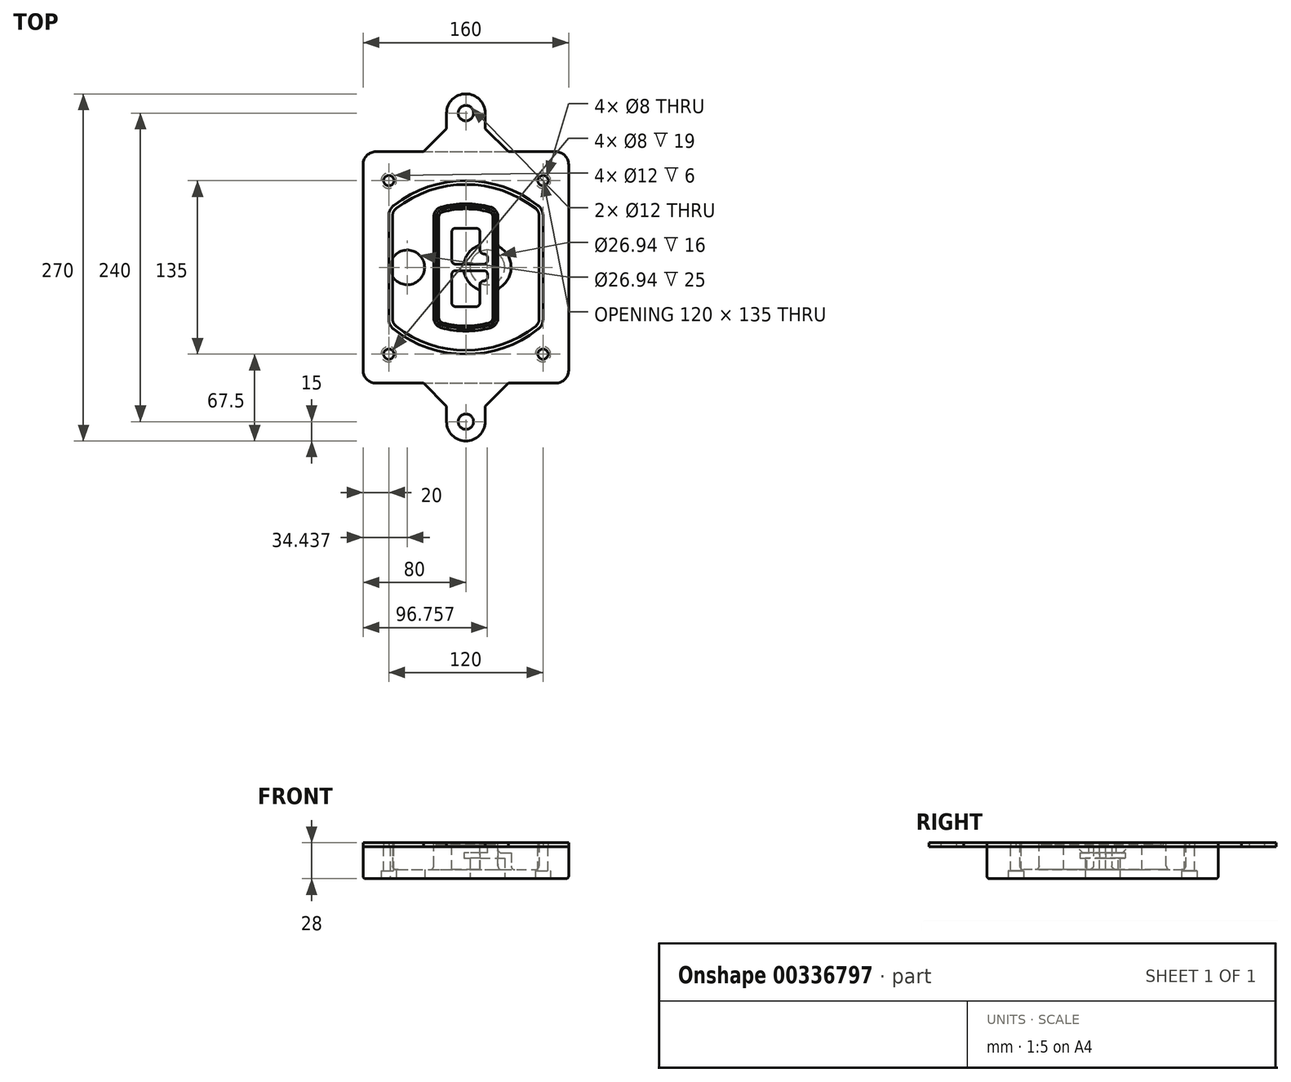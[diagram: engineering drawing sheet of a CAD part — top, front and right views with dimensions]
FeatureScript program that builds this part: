
annotation { "Feature Type Name" : "Feature", "Feature Type Description" : "" }
export const myFeature = defineFeature(function(context is Context, id is Id, definition is map)
    precondition{}
    {
        {
            var Q0;
            Q0=qCreatedBy(makeId("Top.planeOp"),FACE);
            var sketch = newSketch(context, id + "F0", { "sketchPlane" : qUnion([Q0])});
            skPoint(sketch, "E0.rect.middle", {"position": v(0, 0) * mm});
            skLineSegment(sketch, "E1.bottom", {"start": v(-70, -90) * mm, "end": v(70, -90) * mm});
            skLineSegment(sketch, "E1.top", {"start": v(-70, 90) * mm, "end": v(70, 90) * mm});
            skLineSegment(sketch, "E1.left", {"start": v(-80, -80) * mm, "end": v(-80, 80) * mm});
            skLineSegment(sketch, "E1.right", {"start": v(80, -80) * mm, "end": v(80, 80) * mm});
            skLineSegment(sketch, "E2", {"start": v(-80, 90) * mm, "end": v(80, -90) * mm, "construction": true});
            skLineSegment(sketch, "E3", {"start": v(80, 90) * mm, "end": v(-80, -90) * mm, "construction": true});
            skCircle(sketch, "E4", {"center": v(-60, 67.5) * mm, "radius": 4 * mm});
            skCircle(sketch, "E5", {"center": v(60, 67.5) * mm, "radius": 4 * mm});
            skCircle(sketch, "E6", {"center": v(60, -67.5) * mm, "radius": 4 * mm});
            skCircle(sketch, "E7", {"center": v(-60, -67.5) * mm, "radius": 4 * mm});
            skLineSegment(sketch, "E8", {"start": v(-60, 67.5) * mm, "end": v(60, 67.5) * mm, "construction": true});
            skLineSegment(sketch, "E9", {"start": v(60, 67.5) * mm, "end": v(60, -67.5) * mm, "construction": true});
            skLineSegment(sketch, "E10", {"start": v(60, -67.5) * mm, "end": v(-60, -67.5) * mm, "construction": true});
            skLineSegment(sketch, "E11", {"start": v(-60, -67.5) * mm, "end": v(-60, 67.5) * mm, "construction": true});
            skLineSegment(sketch, "E12", {"start": v(-60, 40.3) * mm, "end": v(-60, -40.3) * mm});
            skLineSegment(sketch, "E13", {"start": v(60, 40.3) * mm, "end": v(60, -40.3) * mm});
            skArc(sketch, "E14", {"start": v(56.15, 48.18) * mm, "mid": v(0, 67.5) * mm, "end": v(-56.15, 48.18) * mm});
            skArc(sketch, "E15", {"start": v(-56.15, -48.18) * mm, "mid": v(0, -67.5) * mm, "end": v(56.15, -48.18) * mm});
            skLineSegment(sketch, "E16", {"start": v(-60, 0) * mm, "end": v(60, 0) * mm, "construction": true});
            skPoint(sketch, "E17.visualSharp", {"position": v(-60, -45) * mm});
            skArc(sketch, "E17.filletArc", {"start": v(-60, -40.3) * mm, "mid": v(-58.99, -44.68) * mm, "end": v(-56.15, -48.18) * mm});
            skPoint(sketch, "E18.visualSharp", {"position": v(-60, 45) * mm});
            skArc(sketch, "E18.filletArc", {"start": v(-56.15, 48.18) * mm, "mid": v(-58.99, 44.68) * mm, "end": v(-60, 40.3) * mm});
            skPoint(sketch, "E19.visualSharp", {"position": v(60, 45) * mm});
            skArc(sketch, "E19.filletArc", {"start": v(60, 40.3) * mm, "mid": v(58.99, 44.68) * mm, "end": v(56.15, 48.18) * mm});
            skPoint(sketch, "E20.visualSharp", {"position": v(60, -45) * mm});
            skArc(sketch, "E20.filletArc", {"start": v(56.15, -48.18) * mm, "mid": v(58.99, -44.68) * mm, "end": v(60, -40.3) * mm});
            skPoint(sketch, "E21.visualSharp", {"position": v(-80, 90) * mm});
            skArc(sketch, "E21.filletArc", {"start": v(-70, 90) * mm, "mid": v(-77.07, 87.07) * mm, "end": v(-80, 80) * mm});
            skPoint(sketch, "E22.visualSharp", {"position": v(80, 90) * mm});
            skArc(sketch, "E22.filletArc", {"start": v(80, 80) * mm, "mid": v(77.07, 87.07) * mm, "end": v(70, 90) * mm});
            skPoint(sketch, "E23.visualSharp", {"position": v(80, -90) * mm});
            skArc(sketch, "E23.filletArc", {"start": v(70, -90) * mm, "mid": v(77.07, -87.07) * mm, "end": v(80, -80) * mm});
            skPoint(sketch, "E24.visualSharp", {"position": v(-80, -90) * mm});
            skArc(sketch, "E24.filletArc", {"start": v(-80, -80) * mm, "mid": v(-77.07, -87.07) * mm, "end": v(-70, -90) * mm});
            skArc(sketch, "E25.0", {"start": v(57, 40.3) * mm, "mid": v(56.3, 43.36) * mm, "end": v(54.3, 45.81) * mm});
            skLineSegment(sketch, "E25.1", {"start": v(57, 40.3) * mm, "end": v(57, -40.3) * mm});
            skArc(sketch, "E25.2", {"start": v(54.3, -45.81) * mm, "mid": v(56.3, -43.36) * mm, "end": v(57, -40.3) * mm});
            skArc(sketch, "E25.3", {"start": v(-54.3, -45.81) * mm, "mid": v(0, -64.5) * mm, "end": v(54.3, -45.81) * mm});
            skArc(sketch, "E25.4", {"start": v(-57, -40.3) * mm, "mid": v(-56.3, -43.36) * mm, "end": v(-54.3, -45.81) * mm});
            skArc(sketch, "E25.5", {"start": v(54.3, 45.81) * mm, "mid": v(0, 64.5) * mm, "end": v(-54.3, 45.81) * mm});
            skLineSegment(sketch, "E25.6", {"start": v(-57, 40.3) * mm, "end": v(-57, -40.3) * mm});
            skArc(sketch, "E25.7", {"start": v(-54.3, 45.81) * mm, "mid": v(-56.3, 43.36) * mm, "end": v(-57, 40.3) * mm});
            skArc(sketch, "E26.0", {"start": v(-58.62, 51.33) * mm, "mid": v(-62.58, 46.43) * mm, "end": v(-64, 40.3) * mm});
            skArc(sketch, "E26.1", {"start": v(58.62, 51.33) * mm, "mid": v(0, 71.5) * mm, "end": v(-58.62, 51.33) * mm});
            skArc(sketch, "E26.2", {"start": v(64, 40.3) * mm, "mid": v(62.58, 46.43) * mm, "end": v(58.62, 51.33) * mm});
            skLineSegment(sketch, "E26.3", {"start": v(64, 40.3) * mm, "end": v(64, -40.3) * mm});
            skArc(sketch, "E26.4", {"start": v(58.62, -51.33) * mm, "mid": v(62.58, -46.43) * mm, "end": v(64, -40.3) * mm});
            skLineSegment(sketch, "E26.5", {"start": v(-64, 40.3) * mm, "end": v(-64, -40.3) * mm});
            skArc(sketch, "E26.6", {"start": v(-58.62, -51.33) * mm, "mid": v(0, -71.5) * mm, "end": v(58.62, -51.33) * mm});
            skArc(sketch, "E26.7", {"start": v(-64, -40.3) * mm, "mid": v(-62.58, -46.43) * mm, "end": v(-58.62, -51.33) * mm});
            skSolve(sketch);
        }
        {
            var Q0;
            Q0=makeQuery(id+"F0.imprint","IMPRINT",FACE,{"disambiguationData":[TD([[makeQuery(id+"F0.imprint","IMPRINT",EDGE,{"derivedFrom":sQuery(id+"F0.wireOp",EDGE,"E1.bottom")}),1.0]])]});
            var Q1;
            Q1=makeQuery(id+"F0.imprint","IMPRINT",FACE,{"disambiguationData":[TD([[makeQuery(id+"F0.imprint","IMPRINT",EDGE,{"derivedFrom":sQuery(id+"F0.wireOp",EDGE,"E12")}),1.0]])]});
            var Q2;
            Q2=makeQuery(id+"F0.imprint","IMPRINT",FACE,{"disambiguationData":[TD([[makeQuery(id+"F0.imprint","IMPRINT",EDGE,{"derivedFrom":sQuery(id+"F0.wireOp",EDGE,"E25.0")}),1.0]])]});
            var Q3;
            Q3=makeQuery(id+"F0.imprint","IMPRINT",FACE,{"disambiguationData":[TD([[makeQuery(id+"F0.imprint","IMPRINT",EDGE,{"derivedFrom":sQuery(id+"F0.wireOp",EDGE,"E12")}),-1.0]])]});
            extrude(context, id + "F1", {"entities" : qUnion([Q0, Q1, Q2, Q3]), "oppositeDirection" : true, "depth" : 25 * mm});
        }
        {
            var Q0;
            Q0=makeQuery(id+"F0.imprint","IMPRINT",FACE,{"disambiguationData":[TD([[makeQuery(id+"F0.imprint","IMPRINT",EDGE,{"derivedFrom":sQuery(id+"F0.wireOp",EDGE,"E12")}),1.0]])]});
            extrude(context, id + "F2", {"entities" : qUnion([Q0]), "operationType" : NewBodyOperationType.ADD, "depth" : 3 * mm});
        }
        {
            var Q0;
            Q0=makeQuery(id+"F0.imprint","IMPRINT",FACE,{"disambiguationData":[TD([[makeQuery(id+"F0.imprint","IMPRINT",EDGE,{"derivedFrom":sQuery(id+"F0.wireOp",EDGE,"E25.0")}),1.0]])]});
            extrude(context, id + "F3", {"entities" : qUnion([Q0]), "operationType" : NewBodyOperationType.REMOVE, "oppositeDirection" : true, "depth" : 18 * mm});
        }
        {
            var Q0;
            Q0=makeQuery(id+"F2.opExtrude","CAP_FACE",FACE,{"disambiguationData":[OSD([sQuery(id+"F0.wireOp",EDGE,"E12"),sQuery(id+"F0.wireOp",EDGE,"E13"),sQuery(id+"F0.wireOp",EDGE,"E14"),sQuery(id+"F0.wireOp",EDGE,"E15"),sQuery(id+"F0.wireOp",EDGE,"E17.filletArc"),sQuery(id+"F0.wireOp",EDGE,"E18.filletArc"),sQuery(id+"F0.wireOp",EDGE,"E19.filletArc"),sQuery(id+"F0.wireOp",EDGE,"E20.filletArc"),sQuery(id+"F0.wireOp",EDGE,"E25.0"),sQuery(id+"F0.wireOp",EDGE,"E25.1"),sQuery(id+"F0.wireOp",EDGE,"E25.2"),sQuery(id+"F0.wireOp",EDGE,"E25.3"),sQuery(id+"F0.wireOp",EDGE,"E25.4"),sQuery(id+"F0.wireOp",EDGE,"E25.5"),sQuery(id+"F0.wireOp",EDGE,"E25.6"),sQuery(id+"F0.wireOp",EDGE,"E25.7")])],"isStart":false});
            var sketch = newSketch(context, id + "F4", { "sketchPlane" : qUnion([Q0])});
            skArc(sketch, "E27.0", {"start": v(-19.08, -46.97) * mm, "mid": v(0, -49.5) * mm, "end": v(19.08, -46.97) * mm});
            skArc(sketch, "E28.0", {"start": v(19.08, 46.97) * mm, "mid": v(0, 49.5) * mm, "end": v(-19.08, 46.97) * mm});
            skLineSegment(sketch, "E29", {"start": v(-25, 39.25) * mm, "end": v(-25, -39.25) * mm});
            skLineSegment(sketch, "E30", {"start": v(25, 39.25) * mm, "end": v(25, -39.25) * mm});
            skLineSegment(sketch, "E31", {"start": v(-25, 45.1) * mm, "end": v(25, 45.1) * mm, "construction": true});
            skLineSegment(sketch, "E32", {"start": v(-25, -45.1) * mm, "end": v(25, -45.1) * mm, "construction": true});
            skPoint(sketch, "E33.visualSharp", {"position": v(-25, 45.1) * mm});
            skArc(sketch, "E33.filletArc", {"start": v(-19.08, 46.97) * mm, "mid": v(-23.35, 44.11) * mm, "end": v(-25, 39.25) * mm});
            skPoint(sketch, "E34.visualSharp", {"position": v(25, 45.1) * mm});
            skArc(sketch, "E34.filletArc", {"start": v(25, 39.25) * mm, "mid": v(23.35, 44.11) * mm, "end": v(19.08, 46.97) * mm});
            skPoint(sketch, "E35.visualSharp", {"position": v(25, -45.1) * mm});
            skArc(sketch, "E35.filletArc", {"start": v(19.08, -46.97) * mm, "mid": v(23.35, -44.11) * mm, "end": v(25, -39.25) * mm});
            skPoint(sketch, "E36.visualSharp", {"position": v(-25, -45.1) * mm});
            skArc(sketch, "E36.filletArc", {"start": v(-25, -39.25) * mm, "mid": v(-23.35, -44.11) * mm, "end": v(-19.08, -46.97) * mm});
            skArc(sketch, "E37.0", {"start": v(54.3, 45.81) * mm, "mid": v(0, 64.5) * mm, "end": v(-54.3, 45.81) * mm});
            skArc(sketch, "E37.1", {"start": v(-54.3, 45.81) * mm, "mid": v(-56.3, 43.36) * mm, "end": v(-57, 40.3) * mm});
            skLineSegment(sketch, "E37.2", {"start": v(-57, 40.3) * mm, "end": v(-57, -40.3) * mm});
            skArc(sketch, "E37.3", {"start": v(-57, -40.3) * mm, "mid": v(-56.3, -43.36) * mm, "end": v(-54.3, -45.81) * mm});
            skArc(sketch, "E37.4", {"start": v(-54.3, -45.81) * mm, "mid": v(0, -64.5) * mm, "end": v(54.3, -45.81) * mm});
            skArc(sketch, "E37.5", {"start": v(54.3, -45.81) * mm, "mid": v(56.3, -43.36) * mm, "end": v(57, -40.3) * mm});
            skLineSegment(sketch, "E37.6", {"start": v(57, 40.3) * mm, "end": v(57, -40.3) * mm});
            skArc(sketch, "E37.7", {"start": v(57, 40.3) * mm, "mid": v(56.3, 43.36) * mm, "end": v(54.3, 45.81) * mm});
            skLineSegment(sketch, "E38.0", {"start": v(23, 39.25) * mm, "end": v(23, -39.25) * mm});
            skArc(sketch, "E38.1", {"start": v(18.56, -45.04) * mm, "mid": v(21.76, -42.9) * mm, "end": v(23, -39.25) * mm});
            skArc(sketch, "E38.2", {"start": v(-18.56, -45.04) * mm, "mid": v(0, -47.5) * mm, "end": v(18.56, -45.04) * mm});
            skArc(sketch, "E38.3", {"start": v(-23, -39.25) * mm, "mid": v(-21.76, -42.9) * mm, "end": v(-18.56, -45.04) * mm});
            skLineSegment(sketch, "E38.4", {"start": v(-23, 39.25) * mm, "end": v(-23, -39.25) * mm});
            skArc(sketch, "E38.5", {"start": v(23, 39.25) * mm, "mid": v(21.76, 42.9) * mm, "end": v(18.56, 45.04) * mm});
            skArc(sketch, "E38.6", {"start": v(-18.56, 45.04) * mm, "mid": v(-21.76, 42.9) * mm, "end": v(-23, 39.25) * mm});
            skArc(sketch, "E38.7", {"start": v(18.56, 45.04) * mm, "mid": v(0, 47.5) * mm, "end": v(-18.56, 45.04) * mm});
            skArc(sketch, "E39.0", {"start": v(21, 39.25) * mm, "mid": v(20.18, 41.68) * mm, "end": v(18.04, 43.1) * mm});
            skLineSegment(sketch, "E39.1", {"start": v(21, 39.25) * mm, "end": v(21, -39.25) * mm});
            skArc(sketch, "E39.2", {"start": v(18.04, -43.1) * mm, "mid": v(20.18, -41.68) * mm, "end": v(21, -39.25) * mm});
            skArc(sketch, "E39.3", {"start": v(-18.04, -43.1) * mm, "mid": v(0, -45.5) * mm, "end": v(18.04, -43.1) * mm});
            skArc(sketch, "E39.4", {"start": v(-21, -39.25) * mm, "mid": v(-20.18, -41.68) * mm, "end": v(-18.04, -43.1) * mm});
            skArc(sketch, "E39.5", {"start": v(18.04, 43.1) * mm, "mid": v(0, 45.5) * mm, "end": v(-18.04, 43.1) * mm});
            skLineSegment(sketch, "E39.6", {"start": v(-21, 39.25) * mm, "end": v(-21, -39.25) * mm});
            skArc(sketch, "E39.7", {"start": v(-18.04, 43.1) * mm, "mid": v(-20.18, 41.68) * mm, "end": v(-21, 39.25) * mm});
            skLineSegment(sketch, "E40", {"start": v(-25, 0) * mm, "end": v(25, 0) * mm, "construction": true});
            skLineSegment(sketch, "E41", {"start": v(-11, 5.5) * mm, "end": v(-11, 27.5) * mm});
            skLineSegment(sketch, "E42", {"start": v(-8, 30.5) * mm, "end": v(8, 30.5) * mm});
            skLineSegment(sketch, "E43", {"start": v(11, 27.5) * mm, "end": v(11, 13.5) * mm});
            skLineSegment(sketch, "E44", {"start": v(14, 10.5) * mm, "end": v(14, 10.5) * mm});
            skLineSegment(sketch, "E45", {"start": v(17, 7.5) * mm, "end": v(17, 5.5) * mm});
            skLineSegment(sketch, "E46", {"start": v(14, 2.5) * mm, "end": v(-8, 2.5) * mm});
            skPoint(sketch, "E47.visualSharp", {"position": v(-11, 30.5) * mm});
            skArc(sketch, "E47.filletArc", {"start": v(-8, 30.5) * mm, "mid": v(-10.12, 29.62) * mm, "end": v(-11, 27.5) * mm});
            skPoint(sketch, "E48.visualSharp", {"position": v(11, 30.5) * mm});
            skArc(sketch, "E48.filletArc", {"start": v(11, 27.5) * mm, "mid": v(10.12, 29.62) * mm, "end": v(8, 30.5) * mm});
            skPoint(sketch, "E49.visualSharp", {"position": v(11, 10.5) * mm});
            skArc(sketch, "E49.filletArc", {"start": v(11, 13.5) * mm, "mid": v(11.88, 11.38) * mm, "end": v(14, 10.5) * mm});
            skPoint(sketch, "E50.visualSharp", {"position": v(17, 10.5) * mm});
            skArc(sketch, "E50.filletArc", {"start": v(17, 7.5) * mm, "mid": v(16.12, 9.62) * mm, "end": v(14, 10.5) * mm});
            skPoint(sketch, "E51.visualSharp", {"position": v(17, 2.5) * mm});
            skArc(sketch, "E51.filletArc", {"start": v(14, 2.5) * mm, "mid": v(16.12, 3.38) * mm, "end": v(17, 5.5) * mm});
            skPoint(sketch, "E52.visualSharp", {"position": v(-11, 2.5) * mm});
            skArc(sketch, "E52.filletArc", {"start": v(-11, 5.5) * mm, "mid": v(-10.12, 3.38) * mm, "end": v(-8, 2.5) * mm});
            skLineSegment(sketch, "E53.0.MirrorCS", {"start": v(14, -2.5) * mm, "end": v(-8, -2.5) * mm});
            skArc(sketch, "E54.0.MirrorCS", {"start": v(-11, -5.5) * mm, "mid": v(-10.12, -3.38) * mm, "end": v(-8, -2.5) * mm});
            skLineSegment(sketch, "E55.0.MirrorCS", {"start": v(-11, -5.5) * mm, "end": v(-11, -27.5) * mm});
            skArc(sketch, "E56.0.MirrorCS", {"start": v(-8, -30.5) * mm, "mid": v(-10.12, -29.62) * mm, "end": v(-11, -27.5) * mm});
            skLineSegment(sketch, "E57.0.MirrorCS", {"start": v(-8, -30.5) * mm, "end": v(8, -30.5) * mm});
            skArc(sketch, "E58.0.MirrorCS", {"start": v(11, -27.5) * mm, "mid": v(10.12, -29.62) * mm, "end": v(8, -30.5) * mm});
            skLineSegment(sketch, "E59.0.MirrorCS", {"start": v(11, -27.5) * mm, "end": v(11, -13.5) * mm});
            skArc(sketch, "E60.0.MirrorCS", {"start": v(11, -13.5) * mm, "mid": v(11.88, -11.38) * mm, "end": v(14, -10.5) * mm});
            skArc(sketch, "E61.0.MirrorCS", {"start": v(17, -7.5) * mm, "mid": v(16.12, -9.62) * mm, "end": v(14, -10.5) * mm});
            skLineSegment(sketch, "E62.0.MirrorCS", {"start": v(17, -7.5) * mm, "end": v(17, -5.5) * mm});
            skArc(sketch, "E63.0.MirrorCS", {"start": v(14, -2.5) * mm, "mid": v(16.12, -3.38) * mm, "end": v(17, -5.5) * mm});
            skSolve(sketch);
        }
        {
            var Q0;
            Q0=makeQuery(id+"F4.imprint","IMPRINT",FACE,{"disambiguationData":[TD([[makeQuery(id+"F4.imprint","IMPRINT",EDGE,{"derivedFrom":sQuery(id+"F4.wireOp",EDGE,"E27.0")}),1.0]])]});
            var Q1;
            Q1=makeQuery(id+"F4.imprint","IMPRINT",FACE,{"disambiguationData":[TD([[makeQuery(id+"F4.imprint","IMPRINT",EDGE,{"derivedFrom":sQuery(id+"F4.wireOp",EDGE,"E38.0")}),-1.0]])]});
            var Q2;
            Q2=makeQuery(id+"F4.imprint","IMPRINT",FACE,{"disambiguationData":[TD([[makeQuery(id+"F4.imprint","IMPRINT",EDGE,{"derivedFrom":sQuery(id+"F4.wireOp",EDGE,"E39.0")}),1.0]])]});
            extrude(context, id + "F5", {"entities" : qUnion([Q0, Q1, Q2]), "operationType" : NewBodyOperationType.ADD, "endBound" : BoundingType.UP_TO_NEXT, "oppositeDirection" : true, "depth" : 25 * mm});
        }
        {
            var Q0;
            Q0=makeQuery(id+"F4.imprint","IMPRINT",FACE,{"disambiguationData":[TD([[makeQuery(id+"F4.imprint","IMPRINT",EDGE,{"derivedFrom":sQuery(id+"F4.wireOp",EDGE,"E38.0")}),-1.0]])]});
            extrude(context, id + "F6", {"entities" : qUnion([Q0]), "operationType" : NewBodyOperationType.REMOVE, "oppositeDirection" : true, "depth" : 2 * mm});
        }
        {
            var Q0;
            Q0=makeQuery(id+"F1.opExtrude","CAP_FACE",FACE,{"disambiguationData":[OSD([sQuery(id+"F0.wireOp",EDGE,"E1.bottom"),sQuery(id+"F0.wireOp",EDGE,"E1.top"),sQuery(id+"F0.wireOp",EDGE,"E1.left"),sQuery(id+"F0.wireOp",EDGE,"E1.right"),sQuery(id+"F0.wireOp",EDGE,"E4"),sQuery(id+"F0.wireOp",EDGE,"E5"),sQuery(id+"F0.wireOp",EDGE,"E6"),sQuery(id+"F0.wireOp",EDGE,"E7"),sQuery(id+"F0.wireOp",EDGE,"E21.filletArc"),sQuery(id+"F0.wireOp",EDGE,"E22.filletArc"),sQuery(id+"F0.wireOp",EDGE,"E23.filletArc"),sQuery(id+"F0.wireOp",EDGE,"E24.filletArc")])],"isStart":false});
            var sketch = newSketch(context, id + "F7", { "sketchPlane" : qUnion([Q0])});
            skCircle(sketch, "E64", {"center": v(16.76, 0) * mm, "radius": 13.47 * mm});
            skCircle(sketch, "E65", {"center": v(-45.56, 0) * mm, "radius": 13.47 * mm});
            skLineSegment(sketch, "E66", {"start": v(80, 0) * mm, "end": v(-80, 0) * mm});
            skCircle(sketch, "E67", {"center": v(16.76, 0) * mm, "radius": 18.47 * mm});
            skCircle(sketch, "E68", {"center": v(60, -67.5) * mm, "radius": 6 * mm});
            skCircle(sketch, "E69", {"center": v(-60, -67.5) * mm, "radius": 6 * mm});
            skCircle(sketch, "E70", {"center": v(-60, 67.5) * mm, "radius": 6 * mm});
            skCircle(sketch, "E71", {"center": v(60, 67.5) * mm, "radius": 6 * mm});
            skSolve(sketch);
        }
        {
            var Q0;
            {var subQ1=sQuery(id+"F7.wireOp",EDGE,"E66");var subQ4=sQuery(id+"F7.wireOp",EDGE,"E64");var subQ6=makeQuery(id+"F7.imprint","INTERSECT",VERTEX,{"disambiguationData":[OD(0.0)],"derivedFrom":[subQ4,subQ1]});Q0=makeQuery(id+"F7.imprint","IMPRINT",FACE,{"disambiguationData":[TD([[makeQuery(id+"F7.imprint","IMPRINT",EDGE,{"disambiguationData":[TD([[subQ6,-1.0]])],"derivedFrom":subQ4}),-1.0]])]});}
            var Q1;
            {var subQ0=sQuery(id+"F7.wireOp",EDGE,"E66");var subQ1=sQuery(id+"F7.wireOp",EDGE,"E64");var subQ3=makeQuery(id+"F7.imprint","INTERSECT",VERTEX,{"disambiguationData":[OD(0.0)],"derivedFrom":[subQ1,subQ0]});Q1=makeQuery(id+"F7.imprint","IMPRINT",FACE,{"disambiguationData":[TD([[makeQuery(id+"F7.imprint","IMPRINT",EDGE,{"disambiguationData":[TD([[subQ3,-1.0]])],"derivedFrom":subQ1}),1.0]])]});}
            var Q2;
            {var subQ0=sQuery(id+"F7.wireOp",EDGE,"E66");var subQ1=sQuery(id+"F7.wireOp",EDGE,"E64");var subQ3=makeQuery(id+"F7.imprint","INTERSECT",VERTEX,{"disambiguationData":[OD(0.0)],"derivedFrom":[subQ1,subQ0]});Q2=makeQuery(id+"F7.imprint","IMPRINT",FACE,{"disambiguationData":[TD([[makeQuery(id+"F7.imprint","IMPRINT",EDGE,{"disambiguationData":[TD([[subQ3,1.0]])],"derivedFrom":subQ1}),1.0]])]});}
            var Q3;
            {var subQ1=sQuery(id+"F7.wireOp",EDGE,"E66");var subQ4=sQuery(id+"F7.wireOp",EDGE,"E64");var subQ6=makeQuery(id+"F7.imprint","INTERSECT",VERTEX,{"disambiguationData":[OD(0.0)],"derivedFrom":[subQ4,subQ1]});Q3=makeQuery(id+"F7.imprint","IMPRINT",FACE,{"disambiguationData":[TD([[makeQuery(id+"F7.imprint","IMPRINT",EDGE,{"disambiguationData":[TD([[subQ6,1.0]])],"derivedFrom":subQ4}),-1.0]])]});}
            extrude(context, id + "F8", {"entities" : qUnion([Q0, Q1, Q2, Q3]), "operationType" : NewBodyOperationType.ADD, "oppositeDirection" : true, "depth" : 20 * mm});
        }
        {
            var Q0;
            {var subQ0=sQuery(id+"F7.wireOp",EDGE,"E66");var subQ1=sQuery(id+"F7.wireOp",EDGE,"E64");var subQ3=makeQuery(id+"F7.imprint","INTERSECT",VERTEX,{"disambiguationData":[OD(0.0)],"derivedFrom":[subQ1,subQ0]});Q0=makeQuery(id+"F7.imprint","IMPRINT",FACE,{"disambiguationData":[TD([[makeQuery(id+"F7.imprint","IMPRINT",EDGE,{"disambiguationData":[TD([[subQ3,-1.0]])],"derivedFrom":subQ1}),1.0]])]});}
            var Q1;
            {var subQ0=sQuery(id+"F7.wireOp",EDGE,"E66");var subQ1=sQuery(id+"F7.wireOp",EDGE,"E64");var subQ3=makeQuery(id+"F7.imprint","INTERSECT",VERTEX,{"disambiguationData":[OD(0.0)],"derivedFrom":[subQ1,subQ0]});Q1=makeQuery(id+"F7.imprint","IMPRINT",FACE,{"disambiguationData":[TD([[makeQuery(id+"F7.imprint","IMPRINT",EDGE,{"disambiguationData":[TD([[subQ3,1.0]])],"derivedFrom":subQ1}),1.0]])]});}
            extrude(context, id + "F9", {"entities" : qUnion([Q0, Q1]), "operationType" : NewBodyOperationType.REMOVE, "oppositeDirection" : true, "depth" : 16 * mm});
        }
        {
            var Q0;
            {var subQ0=sQuery(id+"F7.wireOp",EDGE,"E66");var subQ1=sQuery(id+"F7.wireOp",EDGE,"E65");var subQ3=makeQuery(id+"F7.imprint","INTERSECT",VERTEX,{"disambiguationData":[OD(0.0)],"derivedFrom":[subQ1,subQ0]});Q0=makeQuery(id+"F7.imprint","IMPRINT",FACE,{"disambiguationData":[TD([[makeQuery(id+"F7.imprint","IMPRINT",EDGE,{"disambiguationData":[TD([[subQ3,-1.0]])],"derivedFrom":subQ1}),1.0]])]});}
            var Q1;
            {var subQ0=sQuery(id+"F7.wireOp",EDGE,"E66");var subQ1=sQuery(id+"F7.wireOp",EDGE,"E65");var subQ3=makeQuery(id+"F7.imprint","INTERSECT",VERTEX,{"disambiguationData":[OD(0.0)],"derivedFrom":[subQ1,subQ0]});Q1=makeQuery(id+"F7.imprint","IMPRINT",FACE,{"disambiguationData":[TD([[makeQuery(id+"F7.imprint","IMPRINT",EDGE,{"disambiguationData":[TD([[subQ3,1.0]])],"derivedFrom":subQ1}),1.0]])]});}
            extrude(context, id + "F10", {"entities" : qUnion([Q0, Q1]), "operationType" : NewBodyOperationType.REMOVE, "oppositeDirection" : true, "depth" : 25 * mm});
        }
        {
            var Q0;
            Q0=makeQuery(id+"F7.imprint","IMPRINT",FACE,{"disambiguationData":[TD([[makeQuery(id+"F7.imprint","IMPRINT",EDGE,{"derivedFrom":sQuery(id+"F7.wireOp",EDGE,"E68")}),1.0]])]});
            var Q1;
            Q1=makeQuery(id+"F7.imprint","IMPRINT",FACE,{"disambiguationData":[TD([[makeQuery(id+"F7.imprint","IMPRINT",EDGE,{"derivedFrom":makeQuery(id+"F1.opExtrude","CAP_EDGE",EDGE,{"disambiguationData":[OSD([sQuery(id+"F0.wireOp",EDGE,"E5")])],"isStart":false})}),-1.0]])]});
            var Q2;
            Q2=makeQuery(id+"F7.imprint","IMPRINT",FACE,{"disambiguationData":[TD([[makeQuery(id+"F7.imprint","IMPRINT",EDGE,{"derivedFrom":sQuery(id+"F7.wireOp",EDGE,"E69")}),1.0]])]});
            var Q3;
            Q3=makeQuery(id+"F7.imprint","IMPRINT",FACE,{"disambiguationData":[TD([[makeQuery(id+"F7.imprint","IMPRINT",EDGE,{"derivedFrom":makeQuery(id+"F1.opExtrude","CAP_EDGE",EDGE,{"disambiguationData":[OSD([sQuery(id+"F0.wireOp",EDGE,"E4")])],"isStart":false})}),-1.0]])]});
            var Q4;
            Q4=makeQuery(id+"F7.imprint","IMPRINT",FACE,{"disambiguationData":[TD([[makeQuery(id+"F7.imprint","IMPRINT",EDGE,{"derivedFrom":sQuery(id+"F7.wireOp",EDGE,"E70")}),1.0]])]});
            var Q5;
            Q5=makeQuery(id+"F7.imprint","IMPRINT",FACE,{"disambiguationData":[TD([[makeQuery(id+"F7.imprint","IMPRINT",EDGE,{"derivedFrom":makeQuery(id+"F1.opExtrude","CAP_EDGE",EDGE,{"disambiguationData":[OSD([sQuery(id+"F0.wireOp",EDGE,"E7")])],"isStart":false})}),-1.0]])]});
            var Q6;
            Q6=makeQuery(id+"F7.imprint","IMPRINT",FACE,{"disambiguationData":[TD([[makeQuery(id+"F7.imprint","IMPRINT",EDGE,{"derivedFrom":sQuery(id+"F7.wireOp",EDGE,"E71")}),1.0]])]});
            var Q7;
            Q7=makeQuery(id+"F7.imprint","IMPRINT",FACE,{"disambiguationData":[TD([[makeQuery(id+"F7.imprint","IMPRINT",EDGE,{"derivedFrom":makeQuery(id+"F1.opExtrude","CAP_EDGE",EDGE,{"disambiguationData":[OSD([sQuery(id+"F0.wireOp",EDGE,"E6")])],"isStart":false})}),-1.0]])]});
            extrude(context, id + "F11", {"entities" : qUnion([Q0, Q1, Q2, Q3, Q4, Q5, Q6, Q7]), "operationType" : NewBodyOperationType.REMOVE, "oppositeDirection" : true, "depth" : 6 * mm});
        }
        {
            var Q0;
            Q0=makeQuery(id+"F9.boolean.opBoolean","COPY",FACE,{"derivedFrom":makeQuery(id+"F9.opExtrude","CAP_FACE",FACE,{"disambiguationData":[OSD([sQuery(id+"F7.wireOp",EDGE,"E64")])],"isStart":false})});
            var sketch = newSketch(context, id + "F12", { "sketchPlane" : qUnion([Q0])});
            skArc(sketch, "E72.0", {"start": v(11, 17.55) * mm, "mid": v(2.57, 11.82) * mm, "end": v(-1.54, 2.5) * mm});
            skArc(sketch, "E72.1", {"start": v(-1.54, -2.5) * mm, "mid": v(2.57, -11.82) * mm, "end": v(11, -17.55) * mm});
            skLineSegment(sketch, "E73", {"start": v(-1.54, -2.5) * mm, "end": v(14, -2.5) * mm});
            skLineSegment(sketch, "E74.0", {"start": v(14, 2.5) * mm, "end": v(-1.54, 2.5) * mm});
            skArc(sketch, "E74.1", {"start": v(14, 2.5) * mm, "mid": v(16.12, 3.38) * mm, "end": v(17, 5.5) * mm});
            skLineSegment(sketch, "E74.2", {"start": v(17, 7.5) * mm, "end": v(17, 5.5) * mm});
            skArc(sketch, "E74.3", {"start": v(17, 7.5) * mm, "mid": v(16.12, 9.62) * mm, "end": v(14, 10.5) * mm});
            skArc(sketch, "E74.4", {"start": v(11, 13.5) * mm, "mid": v(11.88, 11.38) * mm, "end": v(14, 10.5) * mm});
            skLineSegment(sketch, "E74.5", {"start": v(11, 17.55) * mm, "end": v(11, 13.5) * mm});
            skLineSegment(sketch, "E74.7", {"start": v(14, -2.5) * mm, "end": v(-1.54, -2.5) * mm});
            skArc(sketch, "E74.8", {"start": v(14, -2.5) * mm, "mid": v(16.12, -3.38) * mm, "end": v(17, -5.5) * mm});
            skLineSegment(sketch, "E74.9", {"start": v(17, -7.5) * mm, "end": v(17, -5.5) * mm});
            skArc(sketch, "E74.10", {"start": v(17, -7.5) * mm, "mid": v(16.12, -9.62) * mm, "end": v(14, -10.5) * mm});
            skArc(sketch, "E74.11", {"start": v(11, -13.5) * mm, "mid": v(11.88, -11.38) * mm, "end": v(14, -10.5) * mm});
            skLineSegment(sketch, "E74.12", {"start": v(11, -17.55) * mm, "end": v(11, -13.5) * mm});
            skPoint(sketch, "E75.orphan", {"position": v(11, -27.5) * mm});
            skPoint(sketch, "E76.orphan", {"position": v(-8, -2.5) * mm});
            skPoint(sketch, "E77.orphan", {"position": v(-8, 2.5) * mm});
            skPoint(sketch, "E78.orphan", {"position": v(11, 27.5) * mm});
            skSolve(sketch);
        }
        {
            var Q0;
            {var subQ7=sQuery(id+"F12.wireOp",EDGE,"E72.0");var subQ14=sQuery(id+"F12.wireOp",EDGE,"E72.1");var subQ16=sQuery(id+"F12.wireOp",EDGE,"E74.1");var subQ18=sQuery(id+"F12.wireOp",EDGE,"E74.8");Q0=qUnion([makeQuery(id+"F12.imprint","IMPRINT",FACE,{"disambiguationData":[TD([[makeQuery(id+"F12.imprint","IMPRINT",EDGE,{"derivedFrom":subQ7}),1.0]])]}),makeQuery(id+"F12.imprint","IMPRINT",FACE,{"disambiguationData":[TD([[makeQuery(id+"F12.imprint","IMPRINT",EDGE,{"derivedFrom":subQ14}),1.0]])]}),makeQuery(id+"F12.imprint","IMPRINT",FACE,{"disambiguationData":[TD([[makeQuery(id+"F12.imprint","IMPRINT",EDGE,{"derivedFrom":subQ16}),1.0]])]}),makeQuery(id+"F12.imprint","IMPRINT",FACE,{"disambiguationData":[TD([[makeQuery(id+"F12.imprint","IMPRINT",EDGE,{"derivedFrom":subQ18}),-1.0]])]})]);}
            var Q1;
            Q1=makeQuery(id+"F5.boolean.opBoolean","SPLIT",FACE,{"disambiguationData":[TD([makeQuery(id+"F5.opExtrude","SWEPT_FACE",FACE,{"disambiguationData":[OSD([sQuery(id+"F4.wireOp",EDGE,"E41")])]})])],"derivedFrom":makeQuery(id+"F3.boolean.opBoolean","COPY",FACE,{"derivedFrom":makeQuery(id+"F3.opExtrude","CAP_FACE",FACE,{"disambiguationData":[OSD([sQuery(id+"F0.wireOp",EDGE,"E25.0"),sQuery(id+"F0.wireOp",EDGE,"E25.1"),sQuery(id+"F0.wireOp",EDGE,"E25.2"),sQuery(id+"F0.wireOp",EDGE,"E25.3"),sQuery(id+"F0.wireOp",EDGE,"E25.4"),sQuery(id+"F0.wireOp",EDGE,"E25.5"),sQuery(id+"F0.wireOp",EDGE,"E25.6"),sQuery(id+"F0.wireOp",EDGE,"E25.7")])],"isStart":false})})});
            extrude(context, id + "F13", {"entities" : qUnion([Q0]), "operationType" : NewBodyOperationType.REMOVE, "endBound" : BoundingType.UP_TO_SURFACE, "endBoundEntityFace" : qUnion([Q1]), "depth" : 25 * mm});
        }
        {
            var Q0;
            Q0=makeQuery(id+"F3.boolean.opBoolean","COPY",EDGE,{"derivedFrom":makeQuery(id+"F3.opExtrude","CAP_EDGE",EDGE,{"disambiguationData":[OSD([sQuery(id+"F0.wireOp",EDGE,"E25.6")])],"isStart":false})});
            var Q1;
            Q1=makeQuery(id+"F8.boolean.opBoolean","INTERSECT",EDGE,{"derivedFrom":[makeQuery(id+"F5.opExtrude","SWEPT_FACE",FACE,{"disambiguationData":[OSD([sQuery(id+"F4.wireOp",EDGE,"E30")])]}),makeQuery(id+"F8.opExtrude","CAP_FACE",FACE,{"disambiguationData":[OSD([sQuery(id+"F7.wireOp",EDGE,"E67")])],"isStart":false})]});
            var Q2;
            Q2=makeQuery(id+"F8.boolean.opBoolean","INTERSECT",EDGE,{"disambiguationData":[OD(1.0)],"derivedFrom":[makeQuery(id+"F5.opExtrude","SWEPT_FACE",FACE,{"disambiguationData":[OSD([sQuery(id+"F4.wireOp",EDGE,"E30")])]}),makeQuery(id+"F8.opExtrude","SWEPT_FACE",FACE,{"disambiguationData":[OSD([sQuery(id+"F7.wireOp",EDGE,"E67")])]})]});
            var Q3;
            {var subQ0=sQuery(id+"F4.wireOp",EDGE,"E30");Q3=makeQuery(id+"F8.boolean.opBoolean","SPLIT",EDGE,{"disambiguationData":[TD([makeQuery(id+"F5.opExtrude","SWEPT_FACE",FACE,{"disambiguationData":[OSD([sQuery(id+"F4.wireOp",EDGE,"E35.filletArc")])]})])],"derivedFrom":makeQuery(id+"F5.opExtrude","CAP_EDGE",EDGE,{"disambiguationData":[OSD([subQ0])],"isStart":false})});}
            var Q4;
            {var subQ0=sQuery(id+"F0.wireOp",EDGE,"E25.7");var subQ1=sQuery(id+"F0.wireOp",EDGE,"E25.1");var subQ2=sQuery(id+"F0.wireOp",EDGE,"E25.6");var subQ3=sQuery(id+"F0.wireOp",EDGE,"E25.5");var subQ4=sQuery(id+"F0.wireOp",EDGE,"E25.4");var subQ5=sQuery(id+"F0.wireOp",EDGE,"E25.0");var subQ6=sQuery(id+"F0.wireOp",EDGE,"E25.2");var subQ7=sQuery(id+"F0.wireOp",EDGE,"E25.3");Q4=makeQuery(id+"F8.boolean.opBoolean","INTERSECT",EDGE,{"derivedFrom":[makeQuery(id+"F5.boolean.opBoolean","SPLIT",FACE,{"disambiguationData":[TD([makeQuery(id+"F2.opExtrude","SWEPT_FACE",FACE,{"disambiguationData":[OSD([subQ5])]})])],"derivedFrom":makeQuery(id+"F3.boolean.opBoolean","COPY",FACE,{"derivedFrom":makeQuery(id+"F3.opExtrude","CAP_FACE",FACE,{"disambiguationData":[OSD([subQ5,subQ1,subQ6,subQ7,subQ4,subQ3,subQ2,subQ0])],"isStart":false})})}),makeQuery(id+"F8.opExtrude","SWEPT_FACE",FACE,{"disambiguationData":[OSD([sQuery(id+"F7.wireOp",EDGE,"E67")])]})]});}
            var Q5;
            Q5=makeQuery(id+"F8.boolean.opBoolean","INTERSECT",EDGE,{"disambiguationData":[OD(0.0)],"derivedFrom":[makeQuery(id+"F5.opExtrude","SWEPT_FACE",FACE,{"disambiguationData":[OSD([sQuery(id+"F4.wireOp",EDGE,"E30")])]}),makeQuery(id+"F8.opExtrude","SWEPT_FACE",FACE,{"disambiguationData":[OSD([sQuery(id+"F7.wireOp",EDGE,"E67")])]})]});
            fillet(context, id + "F14", {"entities" : qUnion([Q0, Q1, Q2, Q3, Q4, Q5]), "radius" : 3 * mm, "tangentPropagation" : true, "allowEdgeOverflow" : false});
        }
        {
            var Q0;
            Q0=makeQuery(id+"F1.opExtrude","CAP_EDGE",EDGE,{"disambiguationData":[OSD([sQuery(id+"F0.wireOp",EDGE,"E1.bottom")])],"isStart":false});
            fillet(context, id + "F15", {"entities" : qUnion([Q0]), "radius" : 2 * mm, "tangentPropagation" : true, "allowEdgeOverflow" : false});
        }
        {
            var Q0;
            {var subQ0=sQuery(id+"F0.wireOp",EDGE,"E21.filletArc");var subQ1=sQuery(id+"F0.wireOp",EDGE,"E7");var subQ2=sQuery(id+"F0.wireOp",EDGE,"E6");var subQ3=sQuery(id+"F0.wireOp",EDGE,"E5");var subQ4=sQuery(id+"F0.wireOp",EDGE,"E4");var subQ5=sQuery(id+"F0.wireOp",EDGE,"E22.filletArc");var subQ6=sQuery(id+"F0.wireOp",EDGE,"E1.bottom");var subQ7=sQuery(id+"F0.wireOp",EDGE,"E1.right");var subQ8=sQuery(id+"F0.wireOp",EDGE,"E1.top");var subQ9=sQuery(id+"F0.wireOp",EDGE,"E1.left");var subQ10=sQuery(id+"F0.wireOp",EDGE,"E23.filletArc");var subQ11=sQuery(id+"F0.wireOp",EDGE,"E24.filletArc");Q0=makeQuery(id+"F2.boolean.opBoolean","SPLIT",FACE,{"disambiguationData":[TD([makeQuery(id+"F1.opExtrude","SWEPT_FACE",FACE,{"disambiguationData":[OSD([subQ6])]})])],"derivedFrom":makeQuery(id+"F1.opExtrude","CAP_FACE",FACE,{"disambiguationData":[OSD([subQ6,subQ8,subQ9,subQ7,subQ4,subQ3,subQ2,subQ1,subQ0,subQ5,subQ10,subQ11])],"isStart":true})});}
            var sketch = newSketch(context, id + "F16", { "sketchPlane" : qUnion([Q0])});
            skLineSegment(sketch, "E79", {"start": v(-15, 108) * mm, "end": v(-15, 120) * mm});
            skLineSegment(sketch, "E80", {"start": v(15, 108) * mm, "end": v(15, 120) * mm});
            skLineSegment(sketch, "E81", {"start": v(0, 90) * mm, "end": v(0, 120) * mm, "construction": true});
            skCircle(sketch, "E82", {"center": v(0, 120) * mm, "radius": 6 * mm});
            skArc(sketch, "E83", {"start": v(15, 120) * mm, "mid": v(0, 135) * mm, "end": v(-15, 120) * mm});
            skLineSegment(sketch, "E84", {"start": v(-15, 108) * mm, "end": v(-33, 90) * mm});
            skLineSegment(sketch, "E85", {"start": v(15, 108) * mm, "end": v(33, 90) * mm});
            skLineSegment(sketch, "E86", {"start": v(-80, 0) * mm, "end": v(80, 0) * mm, "construction": true});
            skLineSegment(sketch, "E87.MirrorCS", {"start": v(15, -108) * mm, "end": v(33, -90) * mm});
            skLineSegment(sketch, "E88.MirrorCS", {"start": v(15, -108) * mm, "end": v(15, -120) * mm});
            skArc(sketch, "E89.MirrorCS", {"start": v(15, -120) * mm, "mid": v(0, -135) * mm, "end": v(-15, -120) * mm});
            skCircle(sketch, "E90.MirrorC", {"center": v(0, -120) * mm, "radius": 6 * mm});
            skLineSegment(sketch, "E91.MirrorCS", {"start": v(0, -90) * mm, "end": v(0, -120) * mm, "construction": true});
            skLineSegment(sketch, "E92.MirrorCS", {"start": v(-15, -108) * mm, "end": v(-33, -90) * mm});
            skLineSegment(sketch, "E93.MirrorCS", {"start": v(-15, -108) * mm, "end": v(-15, -120) * mm});
            skSolve(sketch);
        }
        {
            var Q0;
            Q0=makeQuery(id+"F16.imprint","IMPRINT",FACE,{"disambiguationData":[TD([[makeQuery(id+"F16.imprint","IMPRINT",EDGE,{"derivedFrom":sQuery(id+"F16.wireOp",EDGE,"E79")}),-1.0]])]});
            var Q1;
            Q1=makeQuery(id+"F16.imprint","IMPRINT",FACE,{"disambiguationData":[TD([[makeQuery(id+"F16.imprint","IMPRINT",EDGE,{"derivedFrom":makeQuery(id+"F1.opExtrude","CAP_EDGE",EDGE,{"disambiguationData":[OSD([sQuery(id+"F0.wireOp",EDGE,"E4")])],"isStart":true})}),-1.0]])]});
            var Q2;
            {var subQ1=sQuery(id+"F16.wireOp",EDGE,"E87.MirrorCS");Q2=makeQuery(id+"F16.imprint","IMPRINT",FACE,{"disambiguationData":[TD([[makeQuery(id+"F16.imprint","IMPRINT",EDGE,{"derivedFrom":subQ1}),1.0]])]});}
            var Q3;
            Q3=makeQuery(id+"F2.opExtrude","CAP_FACE",FACE,{"disambiguationData":[OSD([sQuery(id+"F0.wireOp",EDGE,"E12"),sQuery(id+"F0.wireOp",EDGE,"E13"),sQuery(id+"F0.wireOp",EDGE,"E14"),sQuery(id+"F0.wireOp",EDGE,"E15"),sQuery(id+"F0.wireOp",EDGE,"E17.filletArc"),sQuery(id+"F0.wireOp",EDGE,"E18.filletArc"),sQuery(id+"F0.wireOp",EDGE,"E19.filletArc"),sQuery(id+"F0.wireOp",EDGE,"E20.filletArc"),sQuery(id+"F0.wireOp",EDGE,"E25.0"),sQuery(id+"F0.wireOp",EDGE,"E25.1"),sQuery(id+"F0.wireOp",EDGE,"E25.2"),sQuery(id+"F0.wireOp",EDGE,"E25.3"),sQuery(id+"F0.wireOp",EDGE,"E25.4"),sQuery(id+"F0.wireOp",EDGE,"E25.5"),sQuery(id+"F0.wireOp",EDGE,"E25.6"),sQuery(id+"F0.wireOp",EDGE,"E25.7")])],"isStart":false});
            extrude(context, id + "F17", {"entities" : qUnion([Q0, Q1, Q2]), "endBound" : BoundingType.UP_TO_SURFACE, "endBoundEntityFace" : qUnion([Q3]), "depth" : 25 * mm});
        }
    });
